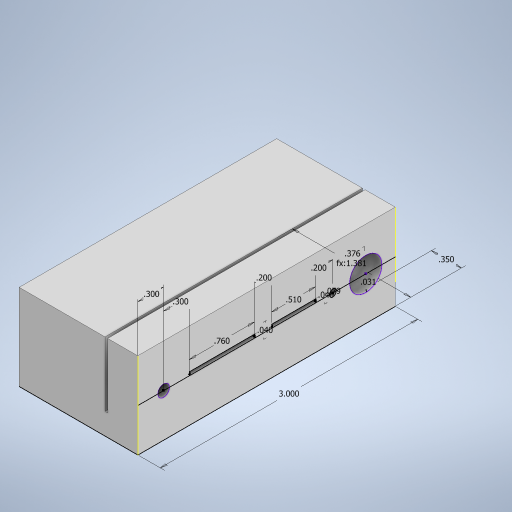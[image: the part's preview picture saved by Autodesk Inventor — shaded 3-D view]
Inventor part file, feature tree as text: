
AUTODESK INVENTOR PART (.ipt)
format: ipt  version: 2023 (Build 270158000, 158)  size: 272,384 bytes
history: native  units: in
note: dims shown in document units (in); Inventor stores cm internally (conversion verified against a paired STEP export)
features: extrude x7, sketch x2
ambient origin geometry x8: Origin, YZ Plane, XZ Plane, XY Plane, X Axis, Y Axis, Z Axis, Center Point
bodies: Solid1 (feature_tree)
feature tree (9):
  sketch  "Sketch1"  dims[d1=3.0in d2=1.3815in]
  extrude  "Extrusion1"  Depth=1.3815in
  extrude  "Extrusion2"  Depth=0.0315in
  extrude  "Extrusion3"  Depth=0.25in TaperAngle=0.0deg
  sketch  "Sketch2"  dims[d3=0.35in d4=0.0315in d5=0.25in d6=0.0in d7=1.0in d8=0.0in d9=1.0in d10=0.0in d11=1.1215in d12=0.0in d13=0.76in d14=0.04in d15=0.51in d16=0.04in d17=1.1015in d18=0.0in d19=0.079in d20=0.7315in d21=0.0in d22=0.3in d23=0.3in d24=0.2in d25=0.2in d26=0.376in d27=0.4425in d28=0.0in]
  extrude  "Extrusion4"  Depth=1.0in TaperAngle=0.0deg
  extrude  "Extrusion5"  Depth=1.0in TaperAngle=0.0deg
  extrude  "Extrusion6"  Depth=1.1215in
  extrude  "Extrusion7"  TaperAngle=0.0deg  [1 undecoded]
note: 1 required parameter value undecoded (feature->parameter linkage not recoverable at this tier; creation-order binding heuristic only, values carry confidence <= 0.55)
